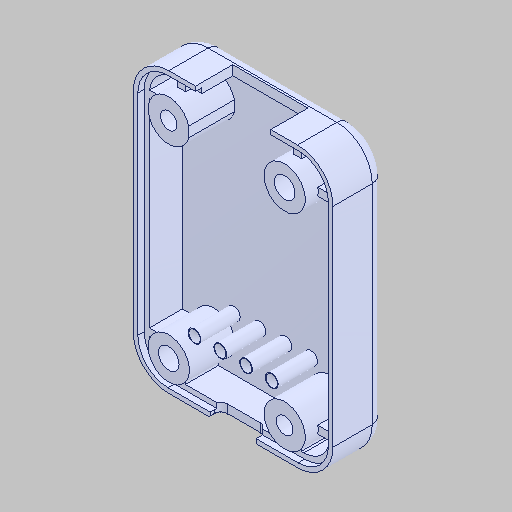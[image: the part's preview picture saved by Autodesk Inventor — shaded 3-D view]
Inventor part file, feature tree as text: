
AUTODESK INVENTOR PART (.ipt)
format: ipt  version: 2023.5 (Build 275446000, 446)  size: 322,560 bytes
history: native  units: in
note: dims shown in document units (in); Inventor stores cm internally (conversion verified against a paired STEP export)
features: fillet x1
ambient origin geometry x8: Origin, YZ Plane, XZ Plane, XY Plane, X Axis, Y Axis, Z Axis, Center Point
bodies: Solid1 (feature_tree)
feature tree (1):
  fillet  "Fillet11"  [1 undecoded]
note: 1 required parameter value undecoded (feature->parameter linkage not recoverable at this tier; creation-order binding heuristic only, values carry confidence <= 0.55)
